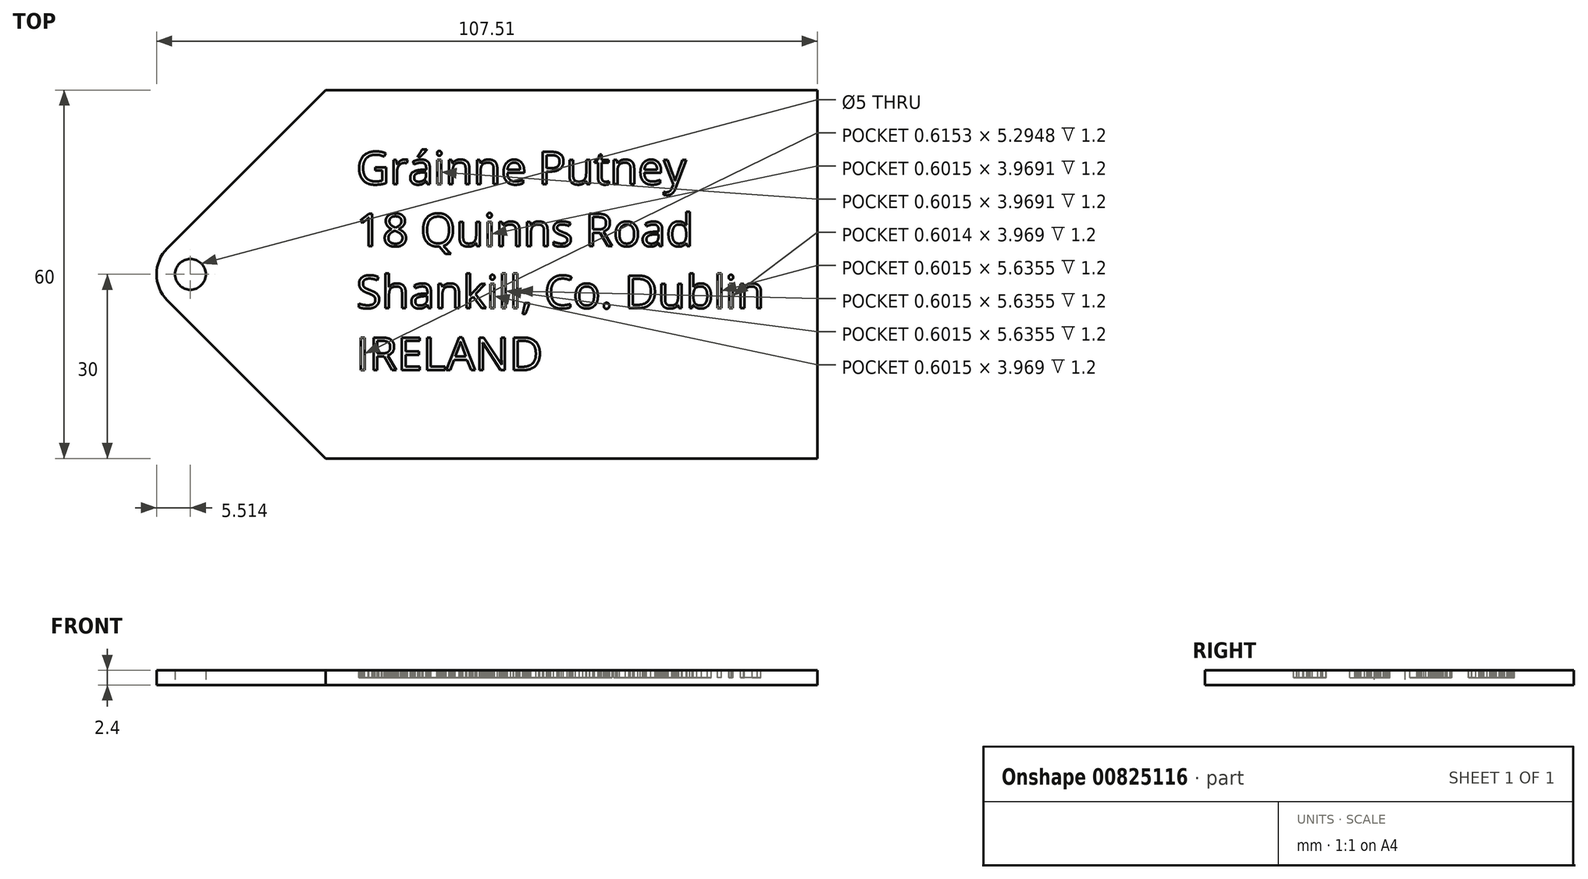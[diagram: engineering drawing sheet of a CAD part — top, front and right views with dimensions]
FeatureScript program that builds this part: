
annotation { "Feature Type Name" : "Feature", "Feature Type Description" : "" }
export const myFeature = defineFeature(function(context is Context, id is Id, definition is map)
    precondition{}
    {
        {
            var Q0;
            Q0=qCreatedBy(makeId("Top.planeOp"),FACE);
            var sketch = newSketch(context, id + "F0", { "sketchPlane" : qUnion([Q0])});
            skLineSegment(sketch, "E0.bottom", {"start": v(-23.87, 30) * mm, "end": v(56.13, 30) * mm});
            skLineSegment(sketch, "E0.top", {"start": v(-23.87, -30) * mm, "end": v(56.13, -30) * mm});
            skLineSegment(sketch, "E0.left", {"start": v(-23.87, 30) * mm, "end": v(-23.87, -30) * mm});
            skLineSegment(sketch, "E0.right", {"start": v(56.13, 30) * mm, "end": v(56.13, -30) * mm});
            skLineSegment(sketch, "E1", {"start": v(-23.87, 30) * mm, "end": v(-49.62, 4.24) * mm});
            skLineSegment(sketch, "E2", {"start": v(-49.62, -4.24) * mm, "end": v(-23.87, -30) * mm});
            skPoint(sketch, "E3.visualSharp", {"position": v(-53.87, 0) * mm});
            skArc(sketch, "E3.filletArc", {"start": v(-49.62, 4.24) * mm, "mid": v(-51.38, 0) * mm, "end": v(-49.62, -4.24) * mm});
            skCircle(sketch, "E4", {"center": v(-45.87, 0) * mm, "radius": 2.5 * mm});
            skSolve(sketch);
        }
        {
            var Q0;
            Q0=makeQuery(id+"F0.imprint","IMPRINT",FACE,{"disambiguationData":[TD([[makeQuery(id+"F0.imprint","IMPRINT",EDGE,{"derivedFrom":sQuery(id+"F0.wireOp",EDGE,"E0.left")}),-1.0]])]});
            var Q1;
            Q1=makeQuery(id+"F0.imprint","IMPRINT",FACE,{"disambiguationData":[TD([[makeQuery(id+"F0.imprint","IMPRINT",EDGE,{"derivedFrom":sQuery(id+"F0.wireOp",EDGE,"E0.bottom")}),-1.0]])]});
            extrude(context, id + "F1", {"entities" : qUnion([Q0, Q1]), "depth" : 2.4 * mm, "offsetDistance" : 25 * mm});
        }
        {
            var Q0;
            Q0=makeQuery(id+"F1.opExtrude","CAP_FACE",FACE,{"disambiguationData":[OSD([sQuery(id+"F0.wireOp",EDGE,"E0.bottom"),sQuery(id+"F0.wireOp",EDGE,"E0.top"),sQuery(id+"F0.wireOp",EDGE,"E0.right"),sQuery(id+"F0.wireOp",EDGE,"E1"),sQuery(id+"F0.wireOp",EDGE,"E2"),sQuery(id+"F0.wireOp",EDGE,"E3.filletArc"),sQuery(id+"F0.wireOp",EDGE,"E4")])],"isStart":false});
            var sketch = newSketch(context, id + "F2", { "sketchPlane" : qUnion([Q0])});
            skText(sketch, "E5", { "text": "Gráinne Putney\n18 Quinns Road\nShankill, Co. Dublin\nIRELAND", "fontName": "OpenSans-Regular.ttf"});
            const initialGuessF2  = {"E5": [-0.01887, 0.01466, 1, 0, 0.00534]};
            skSetInitialGuess(sketch, initialGuessF2);
            skSolve(sketch);
        }
        {
            var Q0;
            Q0=qSketchRegion(id+"F2",true);
            extrude(context, id + "F3", {"entities" : qUnion([Q0]), "operationType" : NewBodyOperationType.REMOVE, "oppositeDirection" : true, "depth" : 1.2 * mm, "offsetDistance" : 25 * mm});
        }
    });
